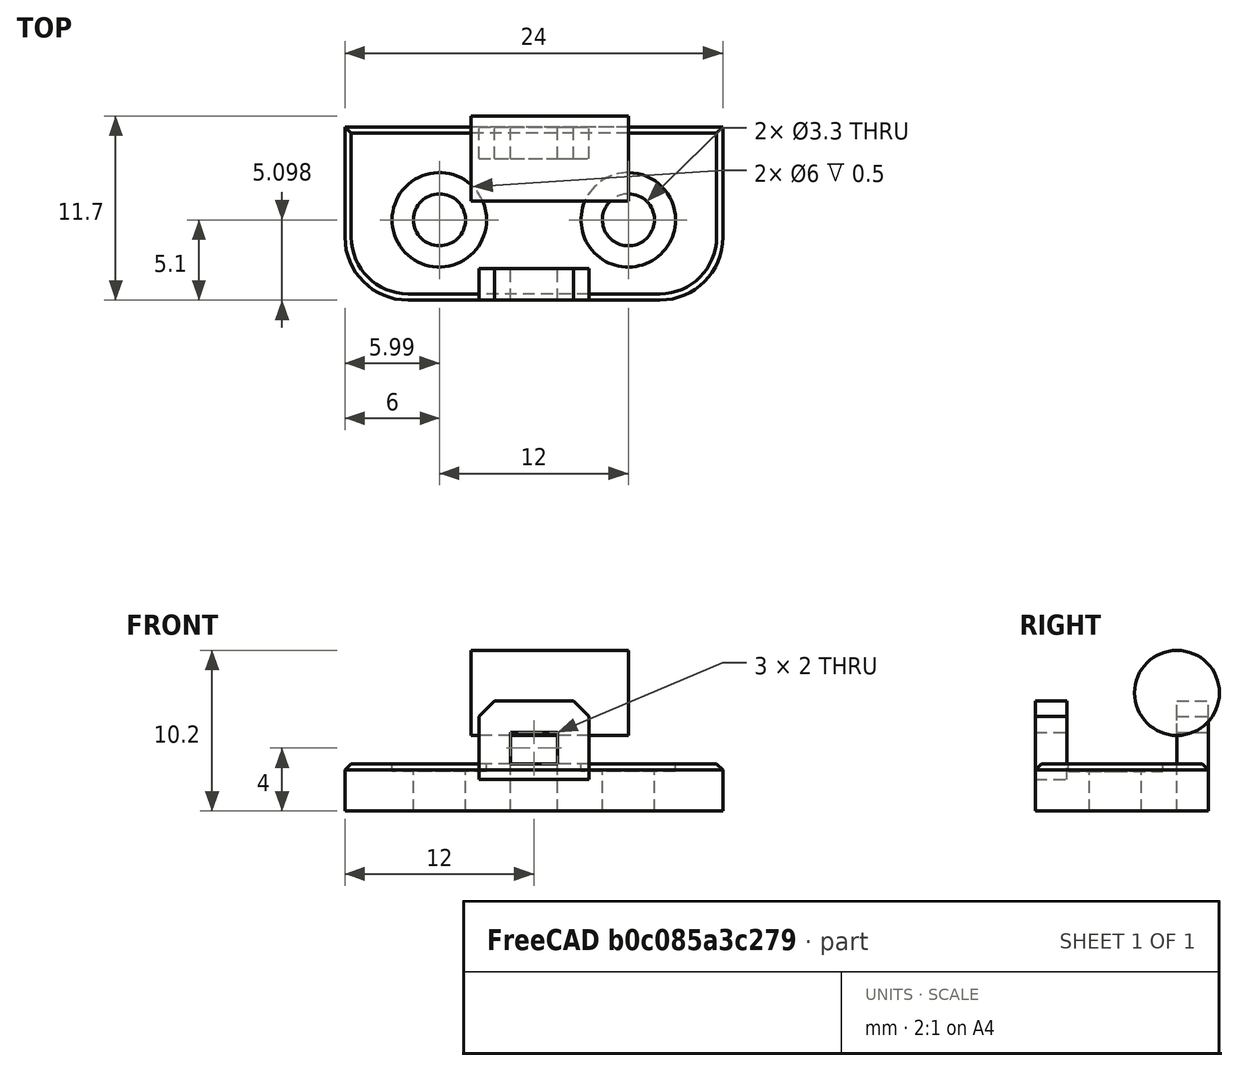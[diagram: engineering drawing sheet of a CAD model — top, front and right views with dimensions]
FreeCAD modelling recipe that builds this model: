
FCSTD DOCUMENT  (FreeCAD 0.18R16146 (Git))
Label: side-wire-mounter
License: All rights reserved
LicenseURL: http://en.wikipedia.org/wiki/All_rights_reserved
objects: Part::Box×4, Part::Cut×3, Part::Cylinder×3, Part::Feature×2, Part::Chamfer×2, Part::MultiFuse×1
note: 15 computed .brp shape members not serialized (recipe doc carries the construction recipe); baked Part::Feature solids carry a one-line shape summary decoded from their .brp

FEATURE [Part::Box] Box  label="Cube"
  AttacherType = Attacher::AttachEngine3D
  Height = 5
  Length = 7
  Placement = pos=(-3.5,-2,2) rot=(0,0,1;0rad)
  Width = 2
FEATURE [Part::Feature] Chamfer007001001  label="base001"
  shape: bbox 24 x 11 x 3 mm, 20 faces (baked)
FEATURE [Part::Box] Box001  label="Cube001"
  AttacherType = Attacher::AttachEngine3D
  Height = 2
  Length = 3
  Placement = pos=(-1.5,-2,3) rot=(0,0,1;0rad)
  Width = 2
FEATURE [Part::Cut] Cut
  Base = -> Box
  Tool = -> Box001
FEATURE [Part::Chamfer] Chamfer
  Base = -> Cut
  Edges = 2 edges r=1: [Edge2,Edge13]
  Placement = pos=(0,-9,0) rot=(0,0,1;0rad)
FEATURE [Part::Cylinder] Cylinder
  Angle = 360
  AttacherType = Attacher::AttachEngine3D
  Height = 10
  Placement = pos=(6,-5.9,0) rot=(0,0,1;0rad)
  Radius = 1.65
FEATURE [Part::Cylinder] Cylinder001
  Angle = 360
  AttacherType = Attacher::AttachEngine3D
  Height = 10
  Placement = pos=(-6,-5.9,0) rot=(0,0,1;0rad)
  Radius = 1.65
FEATURE [Part::MultiFuse] Fusion
  Shapes = -> [Cylinder001,Cylinder]
FEATURE [Part::Cut] Cut001
  Base = -> Chamfer007001001
  Tool = -> Fusion
FEATURE [Part::Feature] Cut001001  label="Cut002"
  shape: bbox 24 x 11 x 3 mm, 20 faces (baked)
FEATURE [Part::Box] Box002  label="Cube002"
  AttacherType = Attacher::AttachEngine3D
  Height = 7
  Length = 7
  Placement = pos=(-3.5,-2,0) rot=(0,0,1;0rad)
  Width = 2
FEATURE [Part::Cylinder] Cylinder002
  Angle = 360
  AttacherType = Attacher::AttachEngine3D
  Height = 10
  Placement = pos=(6,-2,7.5) rot=(0,1,0;4.71239rad)
  Radius = 2.7
FEATURE [Part::Box] Box003  label="Cube003"
  AttacherType = Attacher::AttachEngine3D
  Height = 5
  Length = 3
  Placement = pos=(-1.5,-2,0) rot=(0,0,1;0rad)
  Width = 2
FEATURE [Part::Cut] Cut001002
  Base = -> Box002
  Tool = -> Box003
FEATURE [Part::Chamfer] Chamfer007001002
  Base = -> Cut001002
  Edges = 2 edges r=1: [Edge2,Edge13]
